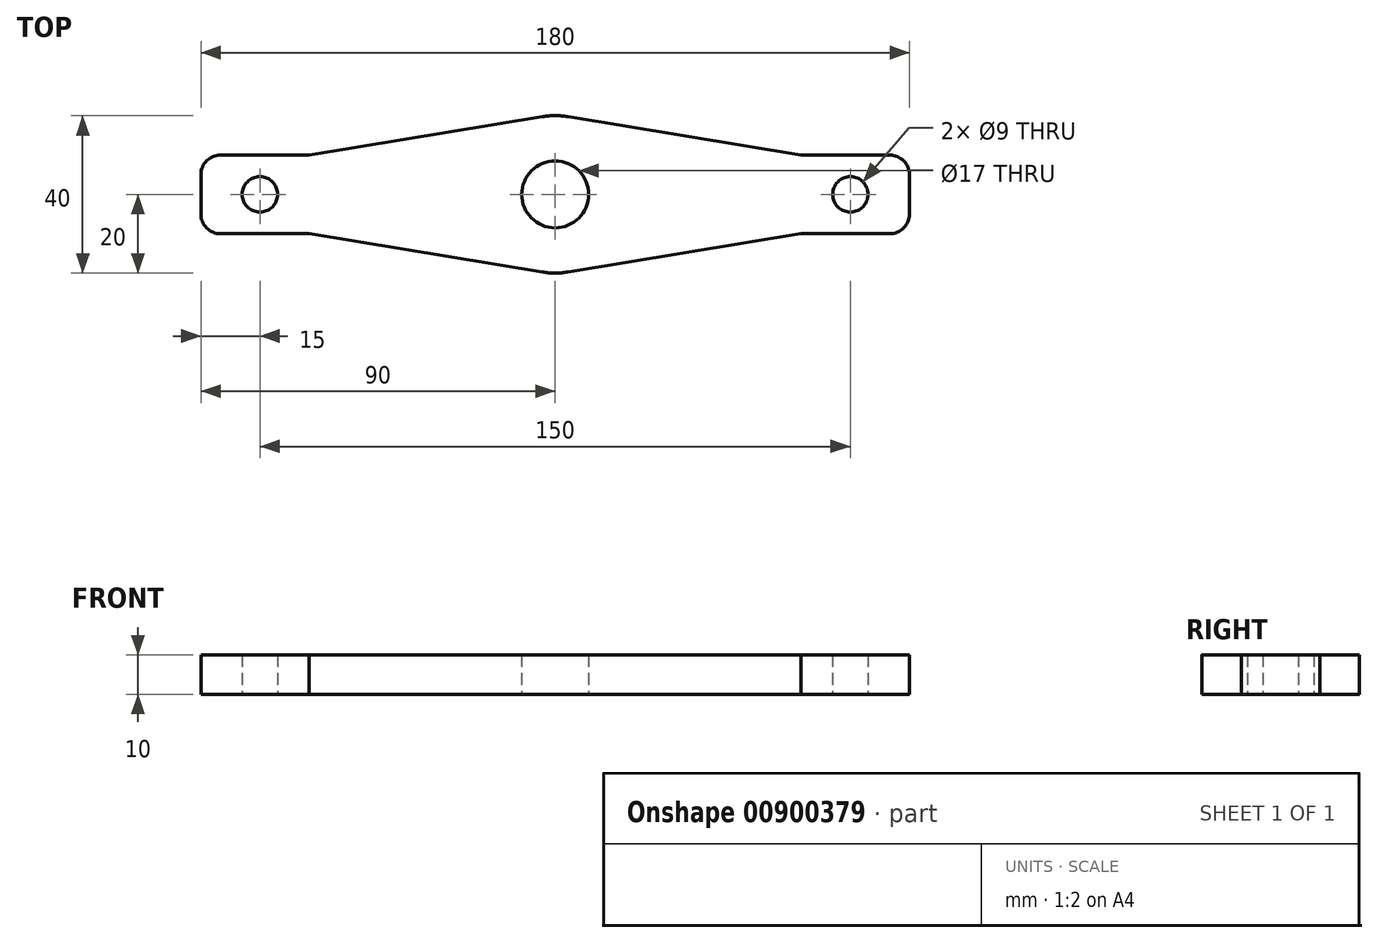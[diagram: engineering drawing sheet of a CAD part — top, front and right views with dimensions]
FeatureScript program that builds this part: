
annotation { "Feature Type Name" : "Feature", "Feature Type Description" : "" }
export const myFeature = defineFeature(function(context is Context, id is Id, definition is map)
    precondition{}
    {
        {
            var Q0;
            Q0=qCreatedBy(makeId("Top.planeOp"),FACE);
            var sketch = newSketch(context, id + "F0", { "sketchPlane" : qUnion([Q0])});
            skLineSegment(sketch, "E0.bottom", {"start": v(-90, 10) * mm, "end": v(90, 10) * mm});
            skLineSegment(sketch, "E0.top", {"start": v(-90, -10) * mm, "end": v(90, -10) * mm});
            skLineSegment(sketch, "E0.left", {"start": v(-90, 10) * mm, "end": v(-90, -10) * mm});
            skLineSegment(sketch, "E0.right", {"start": v(90, 10) * mm, "end": v(90, -10) * mm});
            skPoint(sketch, "E0.middle", {"position": v(0, 0) * mm});
            skCircle(sketch, "E1", {"center": v(0, 0) * mm, "radius": 20 * mm});
            skLineSegment(sketch, "E2", {"start": v(-3.24, 19.74) * mm, "end": v(-62.5, 10) * mm});
            skLineSegment(sketch, "E3", {"start": v(3.24, 19.74) * mm, "end": v(62.5, 10) * mm});
            skLineSegment(sketch, "E4", {"start": v(62.5, -10) * mm, "end": v(3.24, -19.74) * mm});
            skLineSegment(sketch, "E5", {"start": v(-3.24, -19.74) * mm, "end": v(-62.5, -10) * mm});
            skCircle(sketch, "E6", {"center": v(0, 0) * mm, "radius": 8.5 * mm});
            skCircle(sketch, "E7", {"center": v(-75, 0) * mm, "radius": 4.5 * mm});
            skCircle(sketch, "E8", {"center": v(75, 0) * mm, "radius": 4.5 * mm});
            skSolve(sketch);
        }
        {
            var Q0;
            Q0 = qSketchRegion(id + "F0", true);
            var Q1;
            Q1=makeQuery(id+"F0.imprint","IMPRINT",FACE,{"disambiguationData":[TD([[makeQuery(id+"F0.imprint","IMPRINT",EDGE,{"derivedFrom":sQuery(id+"F0.wireOp",EDGE,"E6")}),-1.0]])]});
            extrude(context, id + "F1", {"entities" : qUnion([Q0, Q1]), "depth" : 10 * mm, "offsetDistance" : 25 * mm});
        }
        {
            var Q0;
            Q0=makeQuery(id+"F1.opExtrude","SWEPT_EDGE",EDGE,{"disambiguationData":[OSD([sQuery(id+"F0.wireOp",EDGE,"E0.top"),sQuery(id+"F0.wireOp",EDGE,"E0.left")])]});
            var Q1;
            Q1=makeQuery(id+"F1.opExtrude","SWEPT_EDGE",EDGE,{"disambiguationData":[OSD([sQuery(id+"F0.wireOp",EDGE,"E0.bottom"),sQuery(id+"F0.wireOp",EDGE,"E0.left")])]});
            var Q2;
            Q2=makeQuery(id+"F1.opExtrude","SWEPT_EDGE",EDGE,{"disambiguationData":[OSD([sQuery(id+"F0.wireOp",EDGE,"E0.top"),sQuery(id+"F0.wireOp",EDGE,"E0.right")])]});
            var Q3;
            Q3=makeQuery(id+"F1.opExtrude","SWEPT_EDGE",EDGE,{"disambiguationData":[OSD([sQuery(id+"F0.wireOp",EDGE,"E0.bottom"),sQuery(id+"F0.wireOp",EDGE,"E0.right")])]});
            fillet(context, id + "F2", {"entities" : qUnion([Q0, Q1, Q2, Q3]), "radius" : 5 * mm, "tangentPropagation" : true, "allowEdgeOverflow" : false});
        }
    });
